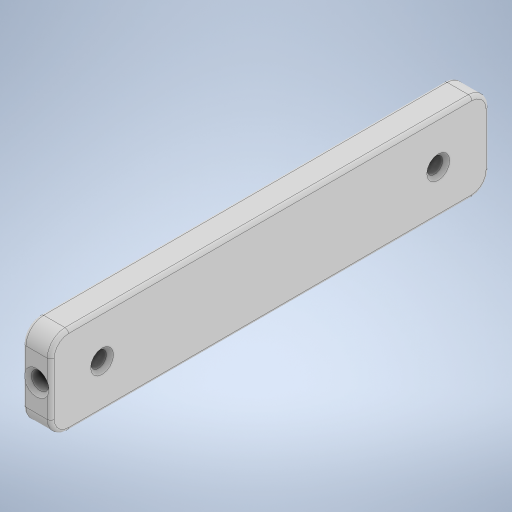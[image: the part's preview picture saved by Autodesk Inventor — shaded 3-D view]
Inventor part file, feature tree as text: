
AUTODESK INVENTOR PART (.ipt)
format: ipt  version: 2023 (Build 270158000, 158)  size: 286,208 bytes
history: native  units: mm
features: extrude x4, sketch x4, fillet x2, chamfer x2
ambient origin geometry x8: Origin, YZ Plane, XZ Plane, XY Plane, X Axis, Y Axis, Z Axis, Center Point
bodies: Volumenkörper1 (feature_tree)
feature tree (12):
  extrude  "Extrusion1"  Depth=8.0mm
  fillet  "Rundung1"  Radius=8.0mm
  extrude  "Extrusion2"  Depth=4.5mm
  extrude  "Extrusion3"  Depth=95.0mm
  extrude  "Extrusion4"  Depth=1.0mm
  chamfer  "Fase1"  Distance=12.5mm
  fillet  "Rundung3"  Radius=5.0mm
  chamfer  "Fase2"  Distance=5.0mm
  sketch  "Skizze1"  dims[d0=25.0mm d1=124.0mm d2=8.0mm d3=0.0mm]
  sketch  "Skizze2"  dims[d4=5.0mm d5=4.5mm]
  sketch  "Skizze3"  dims[d6=4.5mm d7=95.0mm]
  sketch  "Skizze4"  dims[d8=14.5mm d9=12.5mm d10=12.5mm d11=5.0mm d12=0.0mm d14=5.0mm d15=12.5mm d16=4.0mm d17=10.0mm d18=0.0mm d19=10.0mm d20=0.0mm d21=1.0mm d22=2.0mm d23=45.0deg d24=1.0mm d25=1.0mm d26=2.0mm d27=45.0deg]
